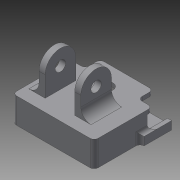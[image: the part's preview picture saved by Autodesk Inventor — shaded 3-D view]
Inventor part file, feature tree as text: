
AUTODESK INVENTOR PART (.ipt)
format: ipt  version: 2013 (Build 170138000, 138)  size: 230,912 bytes
history: native  units: mm
features: extrude x8, sketch x8, fillet x4, mirror x3
ambient origin geometry x8: Origin, YZ Plane, XZ Plane, XY Plane, X Axis, Y Axis, Z Axis, Center Point
bodies: Solid1 (feature_tree)
feature tree (23):
  extrude  "Extrusion1"  Depth=6.35mm
  extrude  "Extrusion2"  Depth=10.0mm
  extrude  "Extrusion3"  Depth=8.5mm TaperAngle=0.0deg
  mirror  "Mirror1"
  extrude  "Extrusion4"  Depth=2.0mm TaperAngle=0.0deg
  mirror  "Mirror2"
  extrude  "Extrusion5"  Depth=2.0mm TaperAngle=0.0deg
  extrude  "Extrusion6"  Depth=12.5mm
  extrude  "Extrusion7"  Depth=12.5mm
  fillet  "Fillet1"  Radius=16.0mm
  fillet  "Fillet2"  Radius=15.0mm
  fillet  "Fillet3"  Radius=3.0mm
  extrude  "Extrusion8"  Depth=14.5mm
  mirror  "Mirror3"
  fillet  "Fillet4"  Radius=17.5mm
  sketch  "Sketch1"  dims[d0=40.0mm d2=6.35mm]
  sketch  "Sketch2"  dims[d4=9.5mm d5=10.0mm]
  sketch  "Sketch4"  dims[d6=20.0mm d7=8.5mm d8=0.0mm]
  sketch  "Sketch5"  dims[d9=20.0mm d10=2.0mm d11=0.0mm]
  sketch  "Sketch6"  dims[d12=6.35mm d13=2.0mm d14=0.0mm]
  sketch  "Sketch7"  dims[d15=7.0mm d17=12.5mm]
  sketch  "Sketch8"  dims[d18=2.0mm d19=0.0mm d20=12.5mm d21=16.0mm d22=0.0mm d23=15.0mm d25=3.0mm]
  sketch  "Sketch9"  dims[d27=5.0mm d28=14.5mm d29=17.5mm d30=0.0mm d31=5.1mm d34=7.5mm d35=10.0mm d36=0.0mm d37=7.5mm d38=4.5mm d39=5.0mm d40=2.0mm d41=2.0mm d42=13.5mm d43=4.0mm d44=0.0mm d45=2.0mm]
